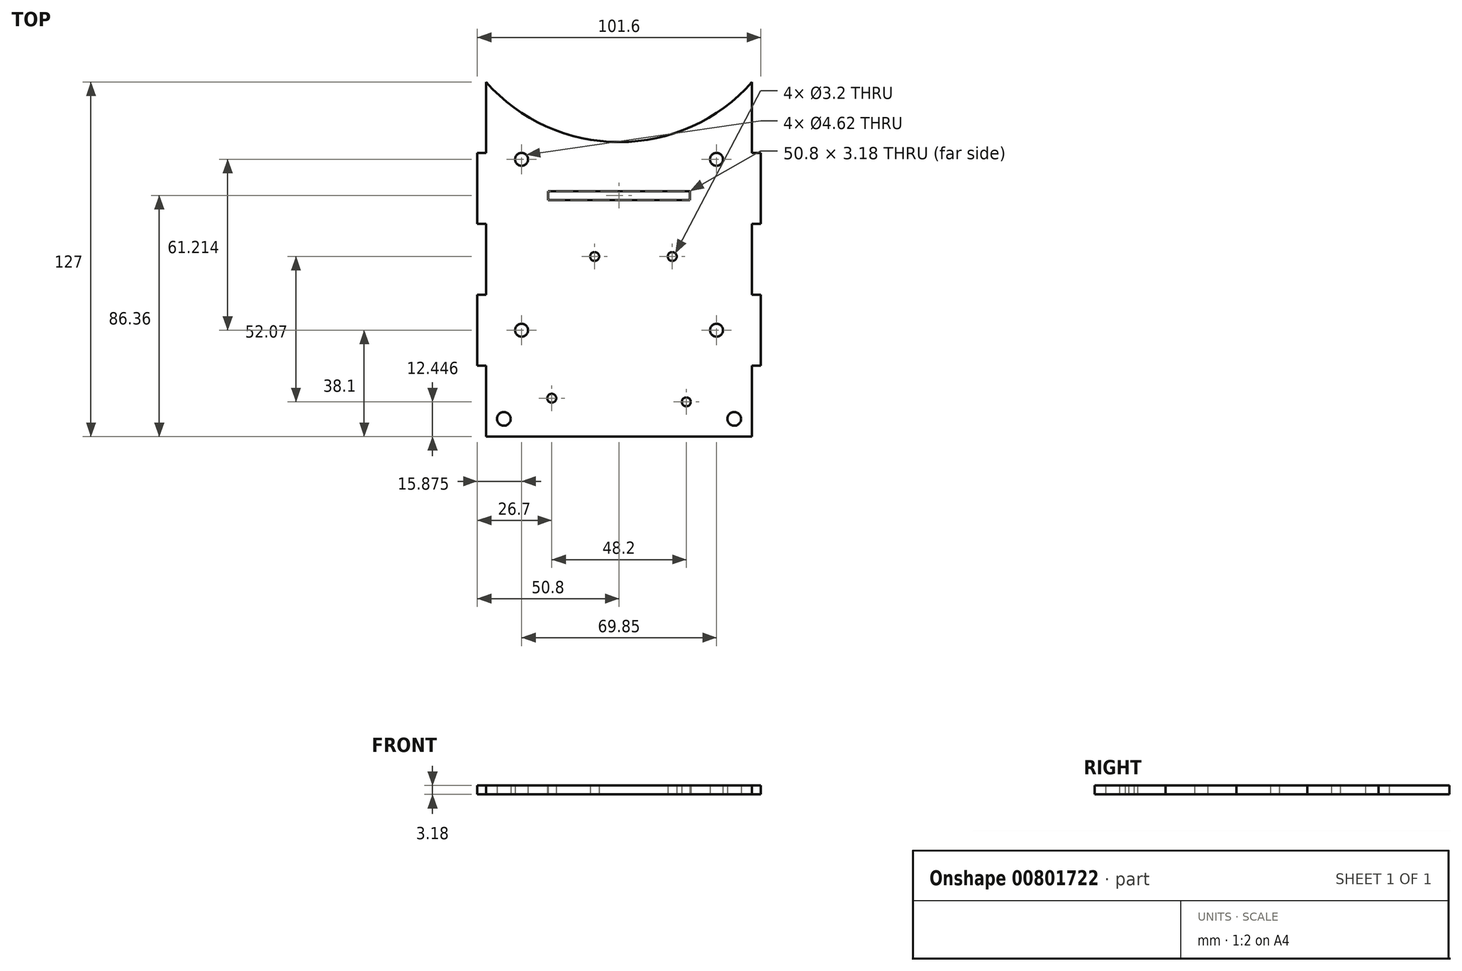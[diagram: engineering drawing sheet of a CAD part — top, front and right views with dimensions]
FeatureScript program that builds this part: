
annotation { "Feature Type Name" : "Feature", "Feature Type Description" : "" }
export const myFeature = defineFeature(function(context is Context, id is Id, definition is map)
    precondition{}
    {
        {
            var Q0;
            Q0=qCreatedBy(makeId("Top.planeOp"),FACE);
            var sketch = newSketch(context, id + "F0", { "sketchPlane" : qUnion([Q0])});
            skLineSegment(sketch, "E0.bottom", {"start": v(47.62, -63.5) * mm, "end": v(-47.63, -63.5) * mm});
            skLineSegment(sketch, "E0.left", {"start": v(47.62, -63.5) * mm, "end": v(47.62, -38.1) * mm});
            skLineSegment(sketch, "E0.right", {"start": v(-47.63, -63.5) * mm, "end": v(-47.63, -38.1) * mm});
            skPoint(sketch, "E0.middle", {"position": v(0, 0) * mm});
            skCircle(sketch, "E1", {"center": v(24.1, -51.05) * mm, "radius": 1.6 * mm});
            skCircle(sketch, "E2.MirrorC", {"center": v(-24.1, -49.76) * mm, "radius": 1.6 * mm});
            skArc(sketch, "E3", {"start": v(-47.63, 63.5) * mm, "mid": v(0, 42) * mm, "end": v(47.63, 63.5) * mm});
            skPoint(sketch, "E4.endSnap0", {"position": v(47.62, 0) * mm});
            skCircle(sketch, "E5", {"center": v(19.05, 1.02) * mm, "radius": 1.6 * mm});
            skCircle(sketch, "E6", {"center": v(-8.76, 1.02) * mm, "radius": 1.6 * mm});
            skLineSegment(sketch, "E7.bottom", {"start": v(47.63, 38.1) * mm, "end": v(50.8, 38.1) * mm});
            skLineSegment(sketch, "E7.top", {"start": v(47.63, 12.7) * mm, "end": v(50.8, 12.7) * mm});
            skLineSegment(sketch, "E7.right", {"start": v(50.8, 38.1) * mm, "end": v(50.8, 12.7) * mm});
            skLineSegment(sketch, "E8.MirrorCS", {"start": v(-50.8, 38.1) * mm, "end": v(-50.8, 12.7) * mm});
            skLineSegment(sketch, "E9.MirrorCS", {"start": v(-47.63, 38.1) * mm, "end": v(-50.8, 38.1) * mm});
            skLineSegment(sketch, "E10.MirrorCS", {"start": v(-47.63, 12.7) * mm, "end": v(-50.8, 12.7) * mm});
            skLineSegment(sketch, "E11.MirrorCS", {"start": v(47.63, -12.7) * mm, "end": v(50.8, -12.7) * mm});
            skLineSegment(sketch, "E12.MirrorCS", {"start": v(50.8, -38.1) * mm, "end": v(50.8, -12.7) * mm});
            skLineSegment(sketch, "E13.MirrorCS", {"start": v(47.63, -38.1) * mm, "end": v(50.8, -38.1) * mm});
            skLineSegment(sketch, "E14.MirrorCS", {"start": v(-47.63, -38.1) * mm, "end": v(-50.8, -38.1) * mm});
            skLineSegment(sketch, "E15.MirrorCS", {"start": v(-47.63, -12.7) * mm, "end": v(-50.8, -12.7) * mm});
            skLineSegment(sketch, "E16.MirrorCS", {"start": v(-50.8, -38.1) * mm, "end": v(-50.8, -12.7) * mm});
            skLineSegment(sketch, "E17.trimOffspring", {"start": v(47.63, 38.1) * mm, "end": v(47.63, 63.5) * mm});
            skLineSegment(sketch, "E18.trimOffspring", {"start": v(47.62, -12.7) * mm, "end": v(47.62, 12.7) * mm});
            skLineSegment(sketch, "E19.trimOffspring", {"start": v(-47.63, -12.7) * mm, "end": v(-47.63, 12.7) * mm});
            skLineSegment(sketch, "E20.trimOffspring", {"start": v(-47.63, 38.1) * mm, "end": v(-47.63, 63.5) * mm});
            skPoint(sketch, "E21.centerSnap0", {"position": v(50.8, 25.4) * mm});
            skCircle(sketch, "E22.MirrorC", {"center": v(34.93, -25.4) * mm, "radius": 2.31 * mm});
            skCircle(sketch, "E23.MirrorC", {"center": v(-34.93, -25.4) * mm, "radius": 2.31 * mm});
            skCircle(sketch, "E24", {"center": v(34.92, 35.81) * mm, "radius": 2.31 * mm});
            skCircle(sketch, "E25", {"center": v(-34.93, 35.81) * mm, "radius": 2.31 * mm});
            skCircle(sketch, "E26", {"center": v(41.27, -57.15) * mm, "radius": 2.46 * mm});
            skCircle(sketch, "E27.MirrorC", {"center": v(-41.27, -57.15) * mm, "radius": 2.46 * mm});
            skLineSegment(sketch, "E28.bottom", {"start": v(25.4, 21.27) * mm, "end": v(-25.4, 21.27) * mm});
            skLineSegment(sketch, "E28.top", {"start": v(25.4, 24.45) * mm, "end": v(-25.4, 24.45) * mm});
            skLineSegment(sketch, "E28.left", {"start": v(25.4, 21.27) * mm, "end": v(25.4, 24.45) * mm});
            skLineSegment(sketch, "E28.right", {"start": v(-25.4, 21.27) * mm, "end": v(-25.4, 24.45) * mm});
            skPoint(sketch, "E28.middle", {"position": v(0, 22.86) * mm});
            skSolve(sketch);
        }
        {
            var Q0;
            Q0 = qSketchRegion(id + "F0", true);
            extrude(context, id + "F1", {"entities" : qUnion([Q0]), "depth" : 3.17 * mm, "offsetDistance" : 25.4 * mm});
        }
    });
